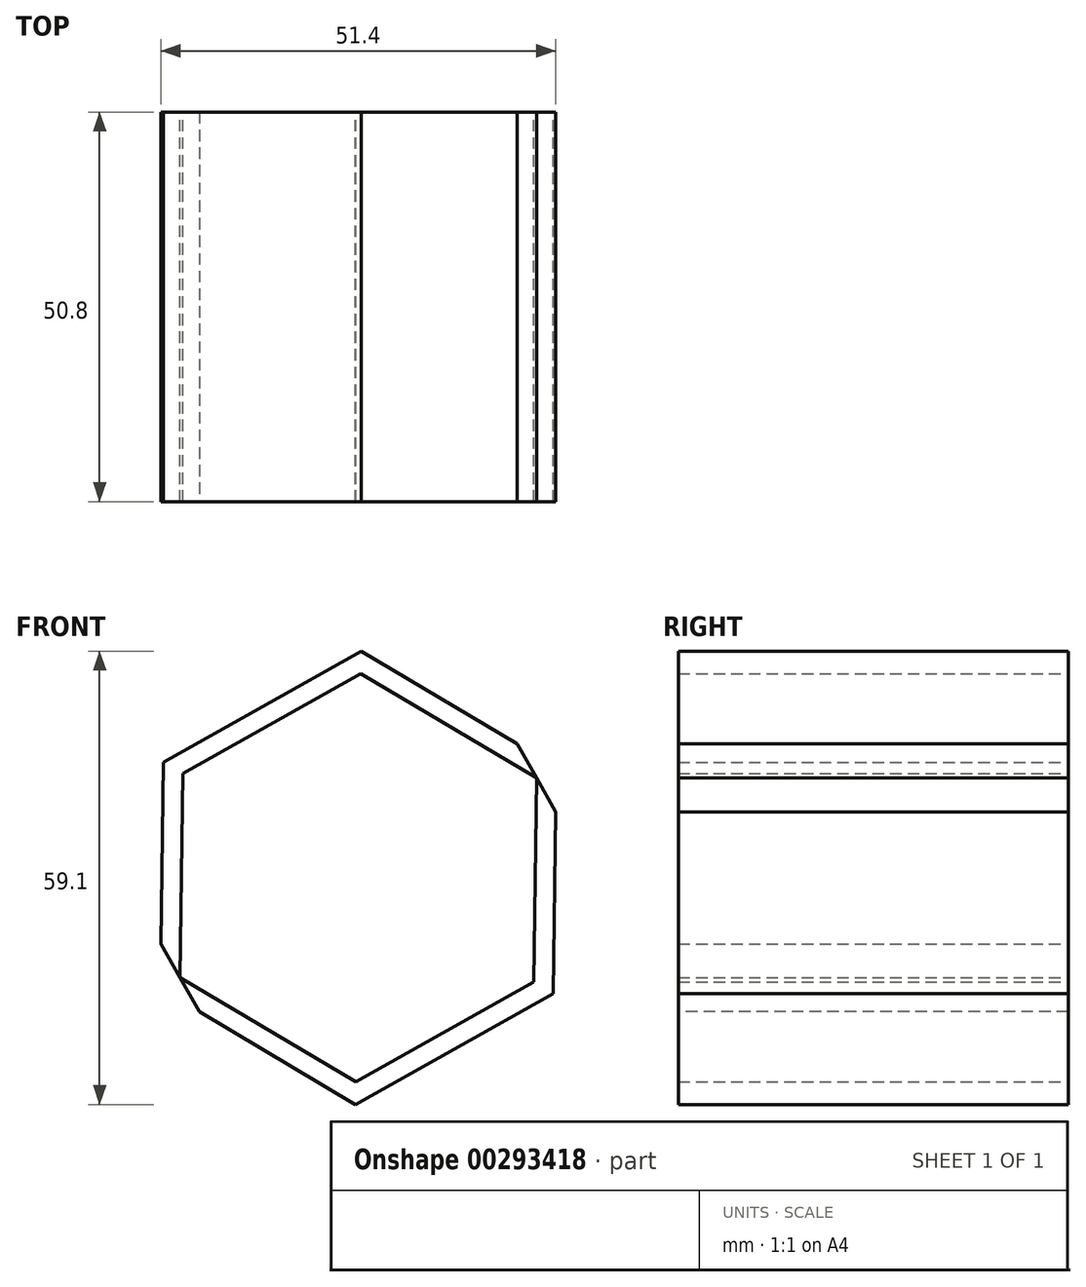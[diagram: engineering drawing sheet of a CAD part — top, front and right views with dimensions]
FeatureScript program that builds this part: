
annotation { "Feature Type Name" : "Feature", "Feature Type Description" : "" }
export const myFeature = defineFeature(function(context is Context, id is Id, definition is map)
    precondition{}
    {
        {
            var Q0;
            Q0=qCreatedBy(makeId("Front.planeOp"),FACE);
            var sketch = newSketch(context, id + "F0", { "sketchPlane" : qUnion([Q0])});
            skCircle(sketch, "E0.cCircle", {"center": v(0, 0) * mm, "radius": 25.59 * mm, "construction": true});
            skLineSegment(sketch, "E0.0", {"start": v(0.37, 29.55) * mm, "end": v(25.77, 14.45) * mm});
            skLineSegment(sketch, "E0.1", {"start": v(25.77, 14.45) * mm, "end": v(25.4, -15.1) * mm});
            skLineSegment(sketch, "E0.2", {"start": v(25.4, -15.1) * mm, "end": v(-0.37, -29.55) * mm});
            skLineSegment(sketch, "E0.3", {"start": v(-0.37, -29.55) * mm, "end": v(-25.77, -14.45) * mm});
            skLineSegment(sketch, "E0.4", {"start": v(-25.77, -14.45) * mm, "end": v(-25.4, 15.1) * mm});
            skLineSegment(sketch, "E0.5", {"start": v(-25.4, 15.1) * mm, "end": v(0.37, 29.55) * mm});
            skPoint(sketch, "E0.0.midPoint", {"position": v(13.07, 22) * mm});
            skPoint(sketch, "E1", {"position": v(-13.78, -11.95) * mm});
            skSolve(sketch);
        }
        {
            var Q0;
            Q0 = qSketchRegion(id + "F0", true);
            extrude(context, id + "F1", {"entities" : qUnion([Q0]), "depth" : 50.8 * mm});
        }
        {
            var Q0;
            Q0=makeQuery(id+"F1.opExtrude","CAP_FACE",FACE,{"disambiguationData":[OSD([sQuery(id+"F0.wireOp",EDGE,"E0.0"),sQuery(id+"F0.wireOp",EDGE,"E0.1"),sQuery(id+"F0.wireOp",EDGE,"E0.2"),sQuery(id+"F0.wireOp",EDGE,"E0.3"),sQuery(id+"F0.wireOp",EDGE,"E0.4"),sQuery(id+"F0.wireOp",EDGE,"E0.5")])],"isStart":true});
            var Q1;
            Q1=makeQuery(id+"F1.opExtrude","CAP_FACE",FACE,{"disambiguationData":[OSD([sQuery(id+"F0.wireOp",EDGE,"E0.0"),sQuery(id+"F0.wireOp",EDGE,"E0.1"),sQuery(id+"F0.wireOp",EDGE,"E0.2"),sQuery(id+"F0.wireOp",EDGE,"E0.3"),sQuery(id+"F0.wireOp",EDGE,"E0.4"),sQuery(id+"F0.wireOp",EDGE,"E0.5")])],"isStart":false});
            shell(context, id + "F2", {"entities" : qUnion([Q0, Q1]), "thickness" : 2.54 * mm});
        }
        {
            var Q0;
            Q0=makeQuery(id+"F2.opShell","OFFSET_FACE",FACE,{"disambiguationData":[OSD([sQuery(id+"F0.wireOp",EDGE,"E0.2")])]});
            var Q1;
            Q1=makeQuery(id+"F2.opShell","OFFSET_FACE",FACE,{"disambiguationData":[OSD([sQuery(id+"F0.wireOp",EDGE,"E0.3")])]});
            var Q2;
            Q2=makeQuery(id+"F2.opShell","OFFSET_FACE",FACE,{"disambiguationData":[OSD([sQuery(id+"F0.wireOp",EDGE,"E0.1")])]});
            var Q3;
            Q3=makeQuery(id+"F2.opShell","OFFSET_FACE",FACE,{"disambiguationData":[OSD([sQuery(id+"F0.wireOp",EDGE,"E0.0")])]});
            var Q4;
            Q4=makeQuery(id+"F2.opShell","OFFSET_FACE",FACE,{"disambiguationData":[OSD([sQuery(id+"F0.wireOp",EDGE,"E0.4")])]});
            var Q5;
            Q5=makeQuery(id+"F2.opShell","OFFSET_FACE",FACE,{"disambiguationData":[OSD([sQuery(id+"F0.wireOp",EDGE,"E0.5")])]});
            extrude(context, id + "F3", {"entities" : qUnion([Q0, Q1, Q2, Q3, Q4, Q5]), "operationType" : NewBodyOperationType.INTERSECT, "endBound" : BoundingType.SYMMETRIC, "oppositeDirection" : true, "depth" : 12.7 * mm});
        }
    });
